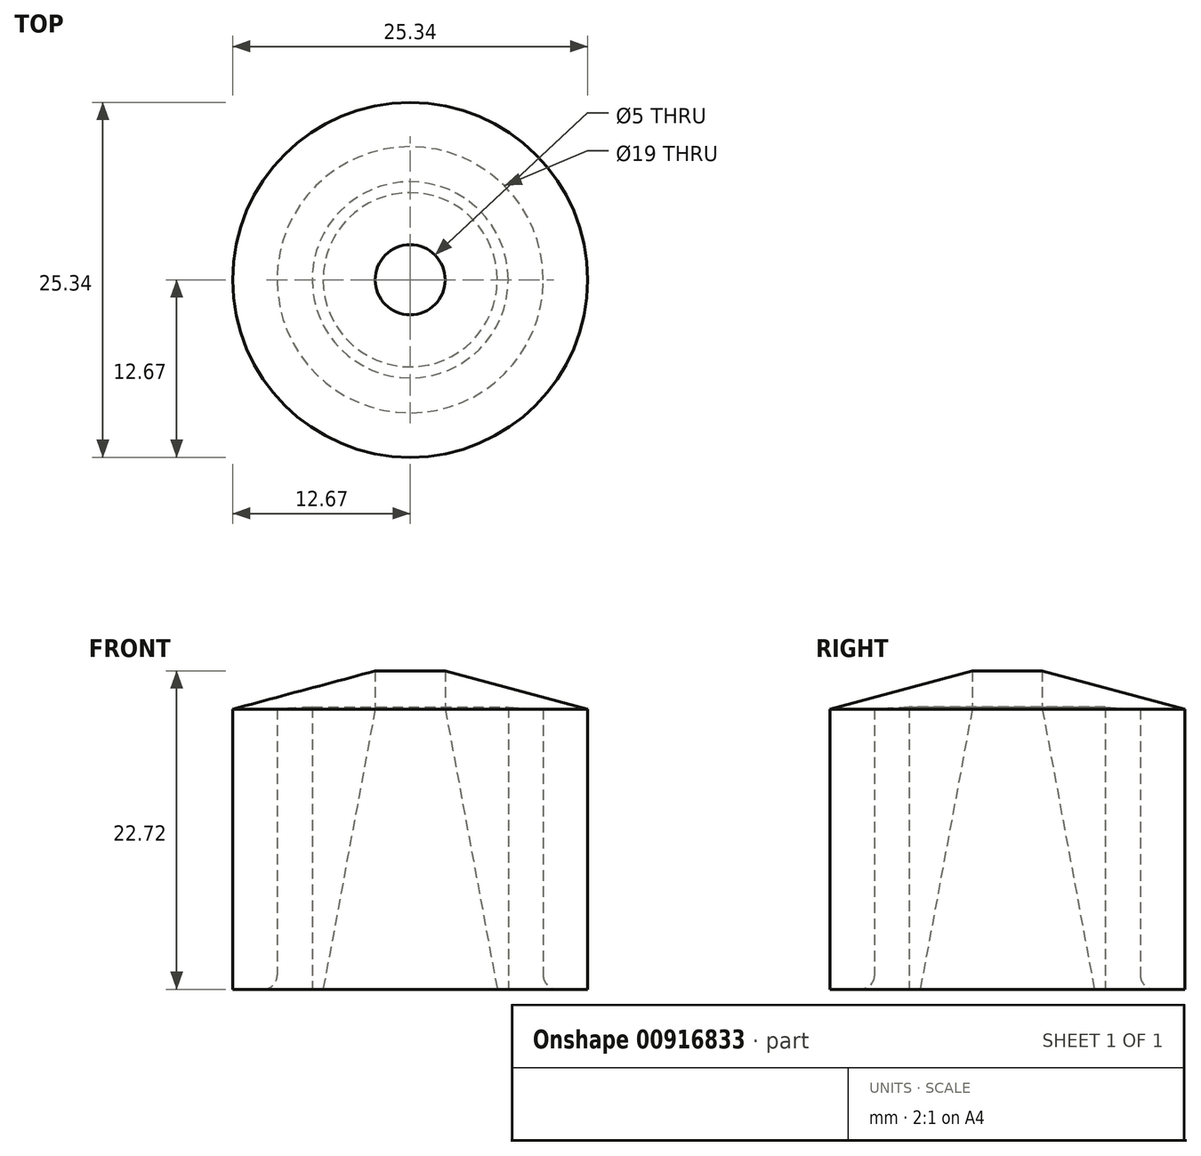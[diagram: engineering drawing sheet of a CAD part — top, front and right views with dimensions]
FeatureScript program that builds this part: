
annotation { "Feature Type Name" : "Feature", "Feature Type Description" : "" }
export const myFeature = defineFeature(function(context is Context, id is Id, definition is map)
    precondition{}
    {
        {
            var Q0;
            Q0=qCreatedBy(makeId("Front.planeOp"),FACE);
            var sketch = newSketch(context, id + "F0", { "sketchPlane" : qUnion([Q0])});
            skPoint(sketch, "E0.center.orphan", {"position": v(-26.77, 26.3) * mm});
            skPoint(sketch, "E1.center.orphan", {"position": v(-38.7, 26.3) * mm});
            skPoint(sketch, "E2.end.orphan", {"position": v(0, 10.7) * mm});
            skPoint(sketch, "E3.end.orphan", {"position": v(0, 320.93) * mm});
            skPoint(sketch, "E3.start.orphan", {"position": v(0, 316.86) * mm});
            skPoint(sketch, "E4.start.orphan", {"position": v(0, 325) * mm});
            skPoint(sketch, "E5.end.orphan", {"position": v(9.5, 0) * mm});
            skPoint(sketch, "E5.start.orphan", {"position": v(7, 0) * mm});
            skLineSegment(sketch, "E6", {"start": v(0, 325) * mm, "end": v(0, 316.86) * mm});
            skLineSegment(sketch, "E7", {"start": v(9.5, 1) * mm, "end": v(9.5, 20) * mm});
            skLineSegment(sketch, "E8", {"start": v(7, 0) * mm, "end": v(7, 20.14) * mm});
            skPoint(sketch, "E9.end.orphan", {"position": v(2.5, 20) * mm});
            skPoint(sketch, "E9.start.orphan", {"position": v(2.5, 0) * mm});
            skPoint(sketch, "E10.start.orphan", {"position": v(12.67, 0) * mm});
            skLineSegment(sketch, "E11", {"start": v(12.67, 0) * mm, "end": v(12.67, 20) * mm});
            skLineSegment(sketch, "E12", {"start": v(10.5, 0) * mm, "end": v(12.67, 0) * mm});
            skLineSegment(sketch, "E13", {"start": v(12.67, 0) * mm, "end": v(11.84, 0) * mm});
            skLineSegment(sketch, "E14", {"start": v(9.5, 20) * mm, "end": v(7, 20.14) * mm});
            skPoint(sketch, "E15.end.orphan", {"position": v(0, 22.83) * mm});
            skPoint(sketch, "E16.end.orphan", {"position": v(0, 21) * mm});
            skPoint(sketch, "E17.end.orphan", {"position": v(0, 20) * mm});
            skLineSegment(sketch, "E18", {"start": v(2.5, 22.72) * mm, "end": v(2.5, 20) * mm});
            skLineSegment(sketch, "E19", {"start": v(2.5, 22.72) * mm, "end": v(12.67, 20) * mm});
            skLineSegment(sketch, "E20", {"start": v(2.5, 20) * mm, "end": v(6.22, 0) * mm});
            skLineSegment(sketch, "E21", {"start": v(7, 0) * mm, "end": v(6.22, 0) * mm});
            skArc(sketch, "E22.filletArc", {"start": v(9.5, 1) * mm, "mid": v(9.8, 0.3) * mm, "end": v(10.5, 0) * mm});
            skLineSegment(sketch, "E23", {"start": v(0, 0) * mm, "end": v(0, 17.3) * mm});
            skSolve(sketch);
        }
        {
            var Q0;
            Q0=makeQuery(id+"F0.imprint","IMPRINT",FACE,{"disambiguationData":[TD([[makeQuery(id+"F0.imprint","IMPRINT",EDGE,{"derivedFrom":sQuery(id+"F0.wireOp",EDGE,"E7")}),-1.0]])]});
            var Q1;
            Q1=sQuery(id+"F0.wireOp",EDGE,"E23");
            revolve(context, id + "F1", {"surfaceOperationType" : NewSurfaceOperationType.NEW, "entities" : qUnion([Q0]), "axis" : qUnion([Q1]), "revolveType" : RevolveType.FULL});
        }
    });
